# Revit family: Ceiling Surface Mount Heaters
name_source: partatom
category: Mechanical Equipment
revit_build: Autodesk Revit 2017 (Build: 20171027_0315(x64)
units: mm (PartAtom-declared; Revit-internal decimal feet)

## family parameters
Always vertical = No
Cut with Voids When Loaded = No
Part Type = Normal
Room Calculation Point = No
Round Connector Dimension = Use Diameter
Shared = No
Work Plane-Based = Yes

## types (16) — shared parameters
Apparent Load = 0 VA
Bezel = 0' - 1"
Default Elevation = 4' - 0"
Frame = Default
Frequency = 0 Hz
Manufacturer = CeramicCircuit Infrared Radiant Heaters
Modeled By = Smith LaRock Architecture | www.slarc.com
Mounting Depth = 0' - 3"
Number of Poles = 1
Panel = Default
Phase = 1
Product Documentation Link = http://192.185.145.162
Product Name = CEILING HEATER SURFACE MOUNTED
Product Page URL = http://electricheat.com
Recess Mount = No
Semi Recess Mount = No
Surface Mount = Yes
URL = http://electricheat.com
Width = 0' - 1 1/8"
zero-valued in all types: Power Factor

## per-type parameters (varying)
| type | Amps | Height | Length | Total Heating Capacity | Voltage | Watts |
| 1445CL - 240V | 6 A | 1' - 3" | 3' - 10" | 5150 Btu/s | 240 V | 1500 W |
| 945CL - 240V | 4 A | 0' - 10" | 3' - 10" | 3414 Btu/s | 240 V | 1000 W |
| 645CL - 240V | 3 A | 0' - 7" | 3' - 10" | 2817 Btu/s | 240 V | 825 W |
| 632CL - 120V | 5 A | 0' - 7" | 2' - 9" | 1989 Btu/s | 120 V | 585 W |
| 632CL - 208V | 3 A | 0' - 7" | 2' - 9" | 1989 Btu/s | 208 V | 585 W |
| 632CL - 240V | 3 A | 0' - 7" | 2' - 9" | 1989 Btu/s | 240 V | 585 W |
| 632CL - 277V | 2 A | 0' - 7" | 2' - 9" | 1989 Btu/s | 277 V | 585 W |
| 645CL - 120V | 7 A | 0' - 7" | 3' - 10" | 2817 Btu/s | 120 V | 825 W |
| 645CL - 208V | 4 A | 0' - 7" | 3' - 10" | 2817 Btu/s | 208 V | 825 W |
| 645CL - 277V | 3 A | 0' - 7" | 3' - 10" | 2817 Btu/s | 277 V | 825 W |
| 945CL - 120V | 8 A | 0' - 10" | 3' - 10" | 3414 Btu/s | 120 V | 1000 W |
| 945CL - 208V | 5 A | 0' - 10" | 3' - 10" | 3414 Btu/s | 208 V | 1000 W |
| 945CL - 277V | 4 A | 0' - 10" | 3' - 10" | 3414 Btu/s | 277 V | 1000 W |
| 1445CL - 120V | 13 A | 1' - 3" | 3' - 10" | 5150 Btu/s | 120 V | 1500 W |
| 1445CL - 208V | 7 A | 1' - 3" | 3' - 10" | 5150 Btu/s | 208 V | 1500 W |
| 1445CL - 277V | 5 A | 1' - 3" | 3' - 10" | 5150 Btu/s | 277 V | 1500 W |

## geometry (parser evidence)
native form markers: Sweep x5
no freeform markers — native parametric forms only
